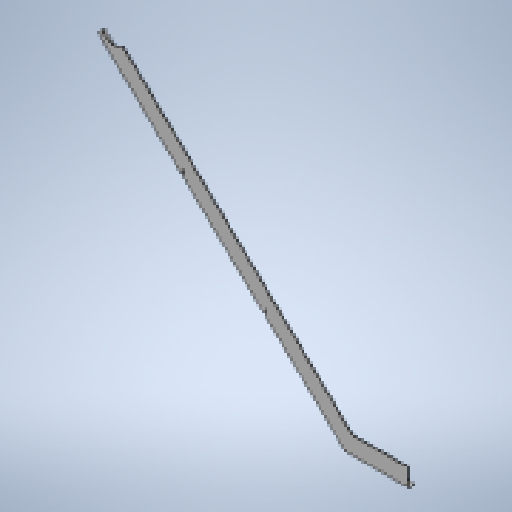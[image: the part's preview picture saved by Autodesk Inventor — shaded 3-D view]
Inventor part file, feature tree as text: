
AUTODESK INVENTOR PART (.ipt)
format: ipt  version: 2025 (Build 290162010, 162A)  size: 410,112 bytes
history: native  units: mm
features: other x6, sheet_metal_op x4, sketch x4, extrude x1, pattern_linear x1
ambient origin geometry x8: Origin, YZ Plane, XZ Plane, XY Plane, X Axis, Y Axis, Z Axis, Center Point
bodies: Body1 (feature_tree)
feature tree (16):
  sheet_metal_op  "Face1"
  sheet_metal_op  "Flange1"
  extrude  "Extrusion2"  Depth=2.75mm
  other  "A-Side Definition"
  pattern_linear  "Rectangular Pattern1"  Spacing1=1.0mm  [1 undecoded]
  other  "Corner Chamfer3"
  other  "Mark2"
  sketch  "Sketch2"  dims[d5=40.0mm d68=2.75mm d91=3.0mm]
  other  "Plate2"
  sketch  "Sketch3"  dims[d95=3.0mm]
  other  "Plate3"
  sheet_metal_op  "Bend2"
  sheet_metal_op  "Corner2"
  sketch  "Sketch5"  dims[d97=2.0mm]
  sketch  "Sketch7"  dims[d98=2.0mm d99=1.0mm d100=4.0mm d101=2.75mm d102=20.0mm d103=90.0deg d104=2.75mm d105=8.0mm d106=0.5mm d107=2.75mm d108=25.0mm d114=30.0mm d115=32.0mm d117=50.0mm d135=12.0mm d139=2.1mm d140=31.0mm d141=5.0mm d142=21.0mm d144=0.0mm d145=0.0mm d146=300.0mm d150=20.0mm d152=300.0mm d153=6.0mm d154=6.0mm d155=45.0deg d156=50.0mm d157=23.736478mm d158=900.0mm d159=140.0mm d160=30.0mm d162=15.0mm]
  other  "Definition1"
note: 1 required parameter value undecoded (feature->parameter linkage not recoverable at this tier; creation-order binding heuristic only, values carry confidence <= 0.55)
